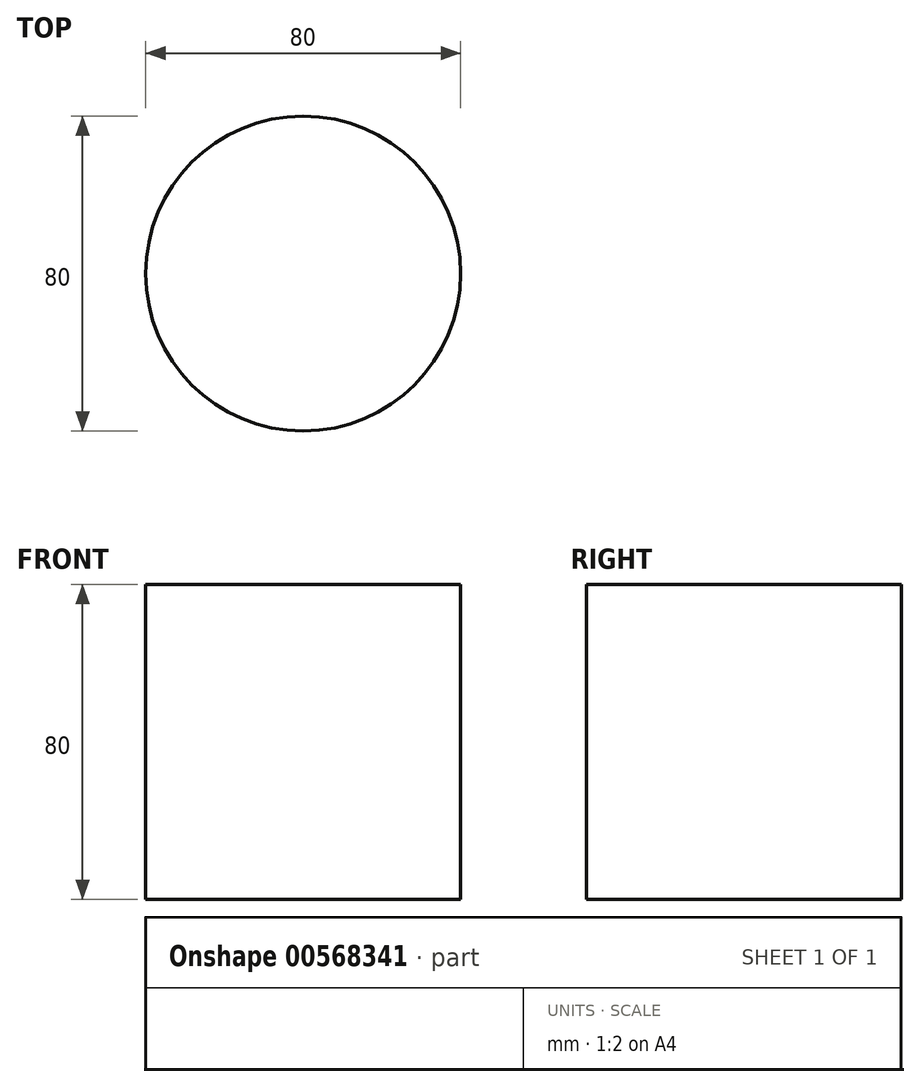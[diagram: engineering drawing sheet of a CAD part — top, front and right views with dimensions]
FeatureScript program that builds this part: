
annotation { "Feature Type Name" : "Feature", "Feature Type Description" : "" }
export const myFeature = defineFeature(function(context is Context, id is Id, definition is map)
    precondition{}
    {
        {
            var Q0;
            Q0=qCreatedBy(makeId("Top.planeOp"),FACE);
            var sketch = newSketch(context, id + "F0", { "sketchPlane" : qUnion([Q0])});
            skCircle(sketch, "E0", {"center": v(0, 0) * mm, "radius": 40 * mm});
            skSolve(sketch);
        }
        {
            var Q0;
            Q0=makeQuery(id+"F0.imprint","IMPRINT",FACE,{"disambiguationData":[TD([[makeQuery(id+"F0.imprint","IMPRINT",EDGE,{"derivedFrom":sQuery(id+"F0.wireOp",EDGE,"E0")}),1.0]])]});
            extrude(context, id + "F1", {"entities" : qUnion([Q0]), "depth" : 80 * mm, "offsetDistance" : 25.4 * mm});
        }
    });
